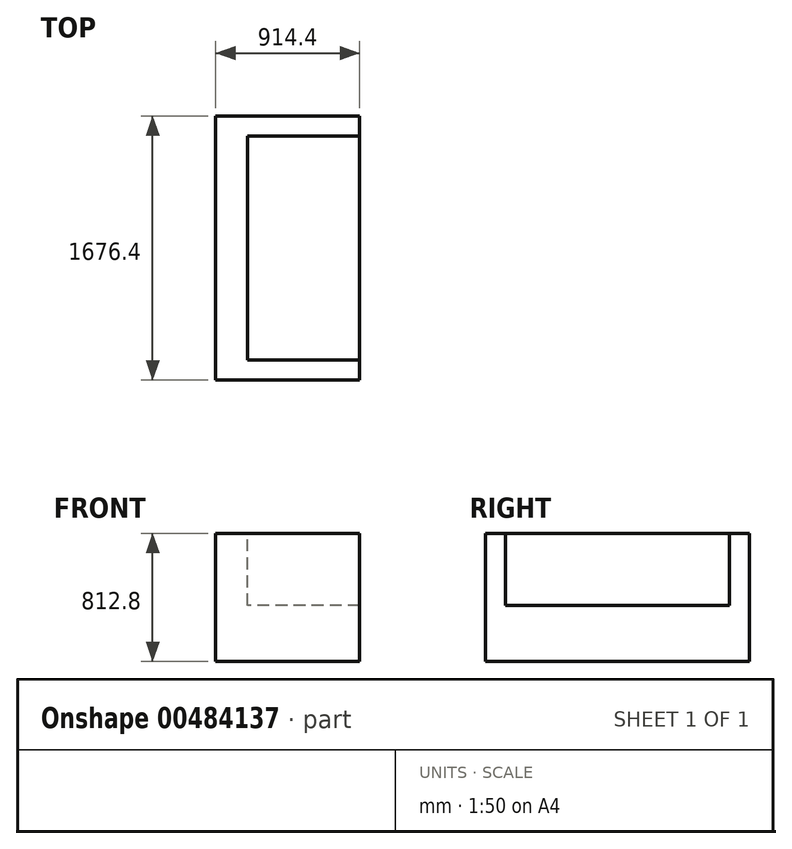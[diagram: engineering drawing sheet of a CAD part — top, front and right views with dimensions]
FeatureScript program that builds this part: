
annotation { "Feature Type Name" : "Feature", "Feature Type Description" : "" }
export const myFeature = defineFeature(function(context is Context, id is Id, definition is map)
    precondition{}
    {
        {
            var Q0;
            Q0=qCreatedBy(makeId("Front.planeOp"),FACE);
            var sketch = newSketch(context, id + "F0", { "sketchPlane" : qUnion([Q0])});
            skLineSegment(sketch, "E0.bottom", {"start": v(0, 0) * mm, "end": v(914.4, 0) * mm});
            skLineSegment(sketch, "E0.top", {"start": v(0, 812.8) * mm, "end": v(914.4, 812.8) * mm});
            skLineSegment(sketch, "E0.left", {"start": v(0, 0) * mm, "end": v(0, 812.8) * mm});
            skLineSegment(sketch, "E0.right", {"start": v(914.4, 0) * mm, "end": v(914.4, 812.8) * mm});
            skSolve(sketch);
        }
        {
            var Q0;
            Q0=qSketchRegion(id+"F0",true);
            extrude(context, id + "F1", {"entities" : qUnion([Q0]), "depth" : 1676.4 * mm});
        }
        {
            var Q0;
            Q0=makeQuery(id+"F1.opExtrude","SWEPT_FACE",FACE,{"disambiguationData":[OSD([sQuery(id+"F0.wireOp",EDGE,"E0.top")])]});
            var sketch = newSketch(context, id + "F2", { "sketchPlane" : qUnion([Q0])});
            skLineSegment(sketch, "E1.bottom", {"start": v(914.4, -127) * mm, "end": v(203.2, -127) * mm});
            skLineSegment(sketch, "E1.top", {"start": v(914.4, -1549.4) * mm, "end": v(203.2, -1549.4) * mm});
            skLineSegment(sketch, "E1.left", {"start": v(914.4, -127) * mm, "end": v(914.4, -1549.4) * mm});
            skLineSegment(sketch, "E1.right", {"start": v(203.2, -127) * mm, "end": v(203.2, -1549.4) * mm});
            skSolve(sketch);
        }
        {
            var Q0;
            Q0 = qSketchRegion(id + "F2", true);
            extrude(context, id + "F3", {"entities" : qUnion([Q0]), "operationType" : NewBodyOperationType.REMOVE, "oppositeDirection" : true, "depth" : 457.2 * mm});
        }
    });
